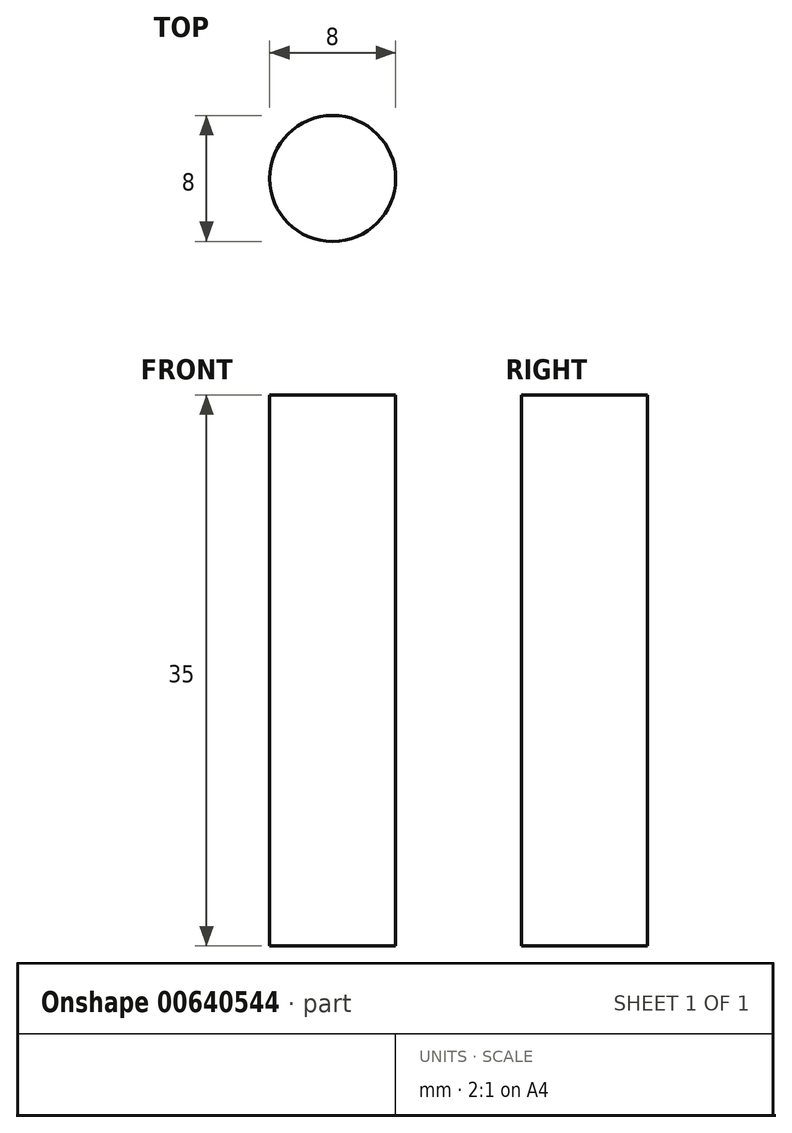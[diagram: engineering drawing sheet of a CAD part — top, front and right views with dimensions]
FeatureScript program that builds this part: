
annotation { "Feature Type Name" : "Feature", "Feature Type Description" : "" }
export const myFeature = defineFeature(function(context is Context, id is Id, definition is map)
    precondition{}
    {
        {
            var Q0;
            Q0=qCreatedBy(makeId("Top.planeOp"),FACE);
            var sketch = newSketch(context, id + "F0", { "sketchPlane" : qUnion([Q0])});
            skCircle(sketch, "E0", {"center": v(0, 0) * mm, "radius": 4 * mm});
            skSolve(sketch);
        }
        {
            var Q0;
            Q0=makeQuery(id+"F0.imprint","IMPRINT",FACE,{"disambiguationData":[TD([[makeQuery(id+"F0.imprint","IMPRINT",EDGE,{"derivedFrom":sQuery(id+"F0.wireOp",EDGE,"E0")}),1.0]])]});
            extrude(context, id + "F1", {"entities" : qUnion([Q0]), "depth" : 35 * mm, "offsetDistance" : 25 * mm});
        }
    });
